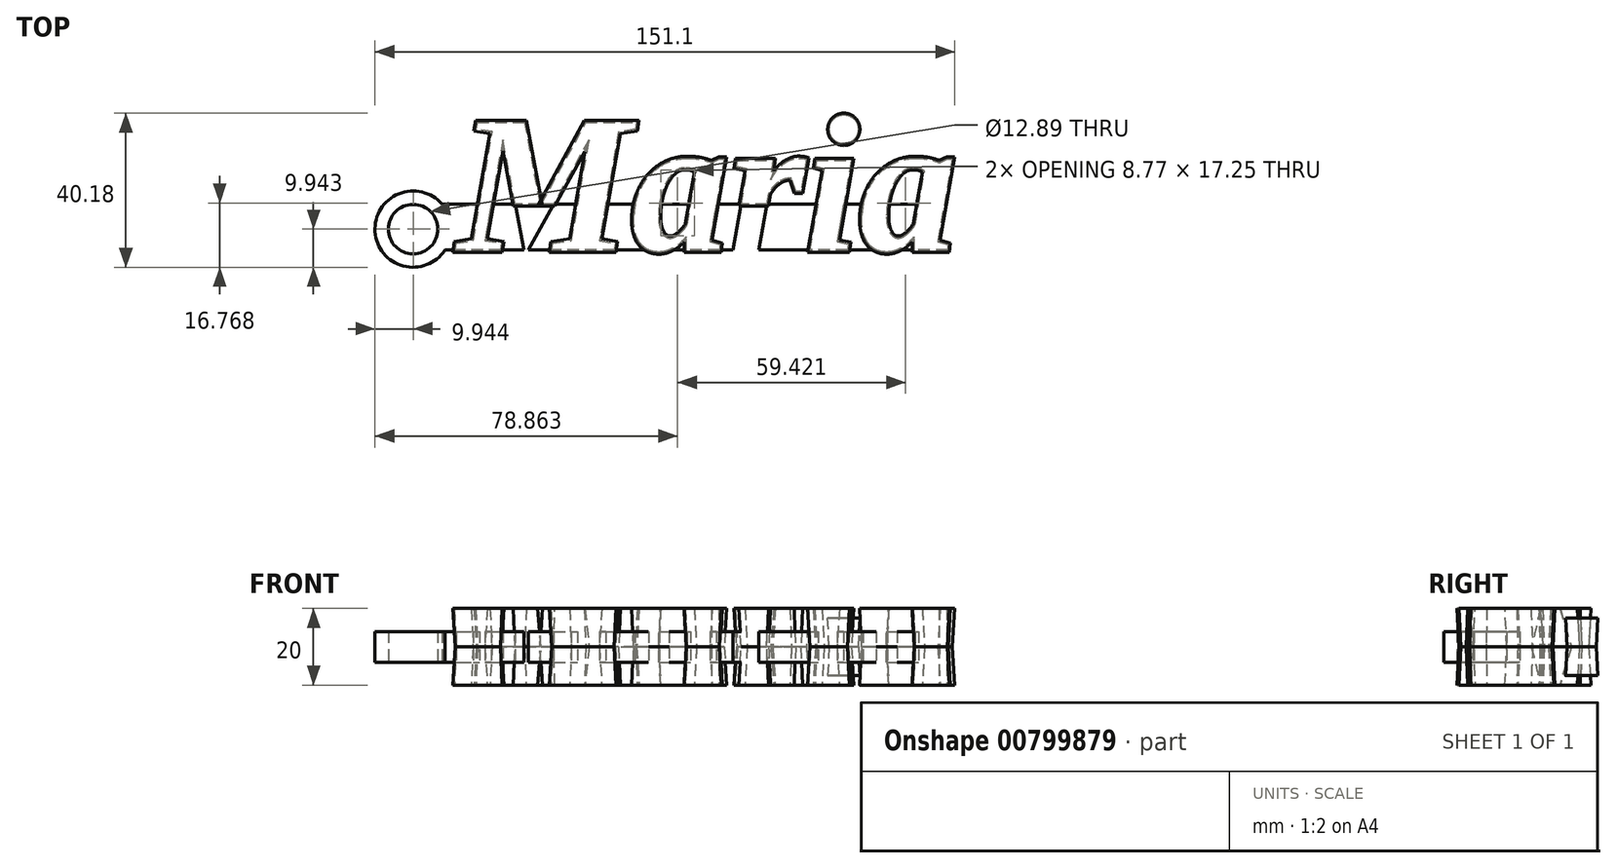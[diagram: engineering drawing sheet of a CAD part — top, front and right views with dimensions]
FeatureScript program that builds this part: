
annotation { "Feature Type Name" : "Feature", "Feature Type Description" : "" }
export const myFeature = defineFeature(function(context is Context, id is Id, definition is map)
    precondition{}
    {
        {
            var Q0;
            Q0=qCreatedBy(makeId("Top.planeOp"),FACE);
            var sketch = newSketch(context, id + "F0", { "sketchPlane" : qUnion([Q0])});
            skLineSegment(sketch, "E0.bottom", {"start": v(-85.5, 0) * mm, "end": v(54.5, 0) * mm});
            skLineSegment(sketch, "E0.top", {"start": v(-85.5, -12) * mm, "end": v(54.5, -12) * mm});
            skLineSegment(sketch, "E0.left", {"start": v(-85.5, 0) * mm, "end": v(-85.5, -12) * mm});
            skLineSegment(sketch, "E0.right", {"start": v(54.5, 0) * mm, "end": v(54.5, -12) * mm});
            skText(sketch, "E1", { "text": "Maria", "fontName": "Tinos-BoldItalic.ttf"});
            skPoint(sketch, "E2.centerSnap0", {"position": v(-82.95, -5.94) * mm});
            skCircle(sketch, "E3", {"center": v(-77.99, -6.52) * mm, "radius": 9.95 * mm});
            skLineSegment(sketch, "E4", {"start": v(32.18, 16.3) * mm, "end": v(31.39, 11.04) * mm});
            skLineSegment(sketch, "E5.0", {"start": v(35.7, 16.13) * mm, "end": v(34.9, 10.85) * mm});
            skCircle(sketch, "E6.0", {"center": v(-77.99, -6.52) * mm, "radius": 6.45 * mm});
            const initialGuessF0  = {"E1": [-0.06639, -0.012, 1, 0, 0.03666]};
            skSetInitialGuess(sketch, initialGuessF0);
            skSolve(sketch);
        }
        {
            var Q0;
            {var subQ5=sQuery(id+"F0.wireOp",EDGE,"E0.left");Q0=makeQuery(id+"F0.imprint","IMPRINT",FACE,{"disambiguationData":[TD([[makeQuery(id+"F0.imprint","IMPRINT",EDGE,{"derivedFrom":subQ5}),1.0]])]});}
            var Q1;
            {var subQ0=sQuery(id+"F0.wireOp",EDGE,"E3");var subQ1=sQuery(id+"F0.wireOp",EDGE,"E0.bottom");var subQ3=makeQuery(id+"F0.imprint","INTERSECT",VERTEX,{"derivedFrom":[subQ1,subQ0]});Q1=makeQuery(id+"F0.imprint","IMPRINT",FACE,{"disambiguationData":[TD([[makeQuery(id+"F0.imprint","IMPRINT",EDGE,{"disambiguationData":[TD([[subQ3,1.0]])],"derivedFrom":subQ1}),1.0]])]});}
            var Q2;
            {var subQ0=sQuery(id+"F0.wireOp",EDGE,"E0.left");Q2=makeQuery(id+"F0.imprint","IMPRINT",FACE,{"disambiguationData":[TD([[makeQuery(id+"F0.imprint","IMPRINT",EDGE,{"derivedFrom":subQ0}),-1.0]])]});}
            var Q3;
            {var subQ1=sQuery(id+"F0.wireOp",EDGE,"E1.sketch_text.stroke-6");Q3=makeQuery(id+"F0.imprint","IMPRINT",FACE,{"disambiguationData":[TD([[makeQuery(id+"F0.imprint","IMPRINT",EDGE,{"derivedFrom":subQ1}),1.0]])]});}
            var Q4;
            {var subQ0=sQuery(id+"F0.wireOp",EDGE,"E1.sketch_text.stroke-3");Q4=makeQuery(id+"F0.imprint","IMPRINT",FACE,{"disambiguationData":[TD([[makeQuery(id+"F0.imprint","IMPRINT",EDGE,{"derivedFrom":subQ0}),1.0]])]});}
            var Q5;
            {var subQ4=sQuery(id+"F0.wireOp",EDGE,"E1.sketch_text.stroke-21");Q5=makeQuery(id+"F0.imprint","IMPRINT",FACE,{"disambiguationData":[TD([[makeQuery(id+"F0.imprint","IMPRINT",EDGE,{"derivedFrom":subQ4}),1.0]])]});}
            var Q6;
            {var subQ0=sQuery(id+"F0.wireOp",EDGE,"E1.sketch_text.stroke-18");Q6=makeQuery(id+"F0.imprint","IMPRINT",FACE,{"disambiguationData":[TD([[makeQuery(id+"F0.imprint","IMPRINT",EDGE,{"derivedFrom":subQ0}),1.0]])]});}
            var Q7;
            {var subQ5=sQuery(id+"F0.wireOp",EDGE,"E1.sketch_text.stroke-40");Q7=makeQuery(id+"F0.imprint","IMPRINT",FACE,{"disambiguationData":[TD([[makeQuery(id+"F0.imprint","IMPRINT",EDGE,{"derivedFrom":subQ5}),1.0]])]});}
            var Q8;
            {var subQ0=sQuery(id+"F0.wireOp",EDGE,"E1.sketch_text.stroke-28");Q8=makeQuery(id+"F0.imprint","IMPRINT",FACE,{"disambiguationData":[TD([[makeQuery(id+"F0.imprint","IMPRINT",EDGE,{"derivedFrom":subQ0}),1.0]])]});}
            var Q9;
            {var subQ1=sQuery(id+"F0.wireOp",EDGE,"E1.sketch_text.stroke-25");Q9=makeQuery(id+"F0.imprint","IMPRINT",FACE,{"disambiguationData":[TD([[makeQuery(id+"F0.imprint","IMPRINT",EDGE,{"derivedFrom":subQ1}),1.0]])]});}
            var Q10;
            {var subQ0=sQuery(id+"F0.wireOp",EDGE,"E1.sketch_text.stroke-57");var subQ1=sQuery(id+"F0.wireOp",EDGE,"E0.bottom");var subQ2=makeQuery(id+"F0.imprint","INTERSECT",VERTEX,{"derivedFrom":[subQ1,subQ0]});Q10=makeQuery(id+"F0.imprint","IMPRINT",FACE,{"disambiguationData":[TD([[makeQuery(id+"F0.imprint","IMPRINT",EDGE,{"disambiguationData":[TD([[subQ2,-1.0]])],"derivedFrom":subQ1}),-1.0]])]});}
            var Q11;
            {var subQ6=sQuery(id+"F0.wireOp",EDGE,"E1.sketch_text.stroke-64");Q11=makeQuery(id+"F0.imprint","IMPRINT",FACE,{"disambiguationData":[TD([[makeQuery(id+"F0.imprint","IMPRINT",EDGE,{"derivedFrom":subQ6}),1.0]])]});}
            var Q12;
            {var subQ0=sQuery(id+"F0.wireOp",EDGE,"E1.sketch_text.stroke-95");Q12=makeQuery(id+"F0.imprint","IMPRINT",FACE,{"disambiguationData":[TD([[makeQuery(id+"F0.imprint","IMPRINT",EDGE,{"derivedFrom":subQ0}),1.0]])]});}
            var Q13;
            {var subQ0=sQuery(id+"F0.wireOp",EDGE,"E1.sketch_text.stroke-83");Q13=makeQuery(id+"F0.imprint","IMPRINT",FACE,{"disambiguationData":[TD([[makeQuery(id+"F0.imprint","IMPRINT",EDGE,{"derivedFrom":subQ0}),1.0]])]});}
            var Q14;
            {var subQ0=sQuery(id+"F0.wireOp",EDGE,"E4");var subQ1=sQuery(id+"F0.wireOp",EDGE,"E1.sketch_text.stroke-70");var subQ2=makeQuery(id+"F0.imprint","INTERSECT",VERTEX,{"derivedFrom":[subQ1,subQ0]});Q14=makeQuery(id+"F0.imprint","IMPRINT",FACE,{"disambiguationData":[TD([[makeQuery(id+"F0.imprint","IMPRINT",EDGE,{"disambiguationData":[TD([[subQ2,-1.0]])],"derivedFrom":subQ1}),1.0]])]});}
            extrude(context, id + "F1", {"entities" : qUnion([Q0, Q1, Q2, Q3, Q4, Q5, Q6, Q7, Q8, Q9, Q10, Q11, Q12, Q13, Q14]), "endBound" : BoundingType.SYMMETRIC, "depth" : 8 * mm, "offsetDistance" : 25 * mm});
        }
        {
            var Q0;
            {var subQ11=sQuery(id+"F0.wireOp",EDGE,"E1.sketch_text.stroke-9");Q0=makeQuery(id+"F0.imprint","IMPRINT",FACE,{"disambiguationData":[TD([[makeQuery(id+"F0.imprint","IMPRINT",EDGE,{"derivedFrom":subQ11}),-1.0]])]});}
            var Q1;
            {var subQ0=sQuery(id+"F0.wireOp",EDGE,"E1.sketch_text.stroke-14");Q1=makeQuery(id+"F0.imprint","IMPRINT",FACE,{"disambiguationData":[TD([[makeQuery(id+"F0.imprint","IMPRINT",EDGE,{"derivedFrom":subQ0}),-1.0]])]});}
            var Q2;
            {var subQ0=sQuery(id+"F0.wireOp",EDGE,"E1.sketch_text.stroke-18");Q2=makeQuery(id+"F0.imprint","IMPRINT",FACE,{"disambiguationData":[TD([[makeQuery(id+"F0.imprint","IMPRINT",EDGE,{"derivedFrom":subQ0}),-1.0]])]});}
            var Q3;
            {var subQ0=sQuery(id+"F0.wireOp",EDGE,"E1.sketch_text.stroke-0");Q3=makeQuery(id+"F0.imprint","IMPRINT",FACE,{"disambiguationData":[TD([[makeQuery(id+"F0.imprint","IMPRINT",EDGE,{"derivedFrom":subQ0}),-1.0]])]});}
            var Q4;
            {var subQ0=sQuery(id+"F0.wireOp",EDGE,"E1.sketch_text.stroke-3");Q4=makeQuery(id+"F0.imprint","IMPRINT",FACE,{"disambiguationData":[TD([[makeQuery(id+"F0.imprint","IMPRINT",EDGE,{"derivedFrom":subQ0}),-1.0]])]});}
            var Q5;
            {var subQ11=sQuery(id+"F0.wireOp",EDGE,"E1.sketch_text.stroke-34");Q5=makeQuery(id+"F0.imprint","IMPRINT",FACE,{"disambiguationData":[TD([[makeQuery(id+"F0.imprint","IMPRINT",EDGE,{"derivedFrom":subQ11}),-1.0]])]});}
            var Q6;
            {var subQ16=sQuery(id+"F0.wireOp",EDGE,"E1.sketch_text.stroke-25");Q6=makeQuery(id+"F0.imprint","IMPRINT",FACE,{"disambiguationData":[TD([[makeQuery(id+"F0.imprint","IMPRINT",EDGE,{"derivedFrom":subQ16}),-1.0]])]});}
            var Q7;
            {var subQ0=sQuery(id+"F0.wireOp",EDGE,"E1.sketch_text.stroke-31");var subQ1=sQuery(id+"F0.wireOp",EDGE,"E0.top");var subQ2=makeQuery(id+"F0.imprint","INTERSECT",VERTEX,{"derivedFrom":[subQ1,subQ0]});Q7=makeQuery(id+"F0.imprint","IMPRINT",FACE,{"disambiguationData":[TD([[makeQuery(id+"F0.imprint","IMPRINT",EDGE,{"disambiguationData":[TD([[subQ2,-1.0]])],"derivedFrom":subQ1}),-1.0]])]});}
            var Q8;
            Q8=makeQuery(id+"F0.imprint","IMPRINT",FACE,{"disambiguationData":[TD([[makeQuery(id+"F0.imprint","IMPRINT",EDGE,{"derivedFrom":sQuery(id+"F0.wireOp",EDGE,"E1.sketch_text.stroke-49")}),-1.0]])]});
            var Q9;
            {var subQ5=sQuery(id+"F0.wireOp",EDGE,"E1.sketch_text.stroke-58");Q9=makeQuery(id+"F0.imprint","IMPRINT",FACE,{"disambiguationData":[TD([[makeQuery(id+"F0.imprint","IMPRINT",EDGE,{"derivedFrom":subQ5}),-1.0]])]});}
            var Q10;
            {var subQ1=sQuery(id+"F0.wireOp",EDGE,"E1.sketch_text.stroke-64");Q10=makeQuery(id+"F0.imprint","IMPRINT",FACE,{"disambiguationData":[TD([[makeQuery(id+"F0.imprint","IMPRINT",EDGE,{"derivedFrom":subQ1}),-1.0]])]});}
            var Q11;
            {var subQ0=sQuery(id+"F0.wireOp",EDGE,"E1.sketch_text.stroke-68");Q11=makeQuery(id+"F0.imprint","IMPRINT",FACE,{"disambiguationData":[TD([[makeQuery(id+"F0.imprint","IMPRINT",EDGE,{"derivedFrom":subQ0}),-1.0]])]});}
            var Q12;
            {var subQ7=sQuery(id+"F0.wireOp",EDGE,"E0.right");Q12=makeQuery(id+"F0.imprint","IMPRINT",FACE,{"disambiguationData":[TD([[makeQuery(id+"F0.imprint","IMPRINT",EDGE,{"derivedFrom":subQ7}),-1.0]])]});}
            var Q13;
            {var subQ2=sQuery(id+"F0.wireOp",EDGE,"E0.right");Q13=makeQuery(id+"F0.imprint","IMPRINT",FACE,{"disambiguationData":[TD([[makeQuery(id+"F0.imprint","IMPRINT",EDGE,{"derivedFrom":subQ2}),1.0]])]});}
            var Q14;
            {var subQ0=sQuery(id+"F0.wireOp",EDGE,"E1.sketch_text.stroke-86");var subQ1=sQuery(id+"F0.wireOp",EDGE,"E0.top");var subQ2=makeQuery(id+"F0.imprint","INTERSECT",VERTEX,{"derivedFrom":[subQ1,subQ0]});Q14=makeQuery(id+"F0.imprint","IMPRINT",FACE,{"disambiguationData":[TD([[makeQuery(id+"F0.imprint","IMPRINT",EDGE,{"disambiguationData":[TD([[subQ2,-1.0]])],"derivedFrom":subQ1}),-1.0]])]});}
            extrude(context, id + "F2", {"entities" : qUnion([Q0, Q1, Q2, Q3, Q4, Q5, Q6, Q7, Q8, Q9, Q10, Q11, Q12, Q13, Q14]), "endBound" : BoundingType.SYMMETRIC, "depth" : 20 * mm, "offsetDistance" : 25 * mm, "hasDraft" : true, "draftAngle" : 3 * degree});
        }
        {
            var Q0;
            Q0=makeQuery(id+"F0.imprint","IMPRINT",FACE,{"disambiguationData":[TD([[makeQuery(id+"F0.imprint","IMPRINT",EDGE,{"derivedFrom":sQuery(id+"F0.wireOp",EDGE,"E1.sketch_text.stroke-72")}),-1.0]])]});
            extrude(context, id + "F3", {"entities" : qUnion([Q0]), "endBound" : BoundingType.SYMMETRIC, "depth" : 15 * mm, "offsetDistance" : 25 * mm, "hasDraft" : true, "draftAngle" : 3 * degree});
        }
    });
